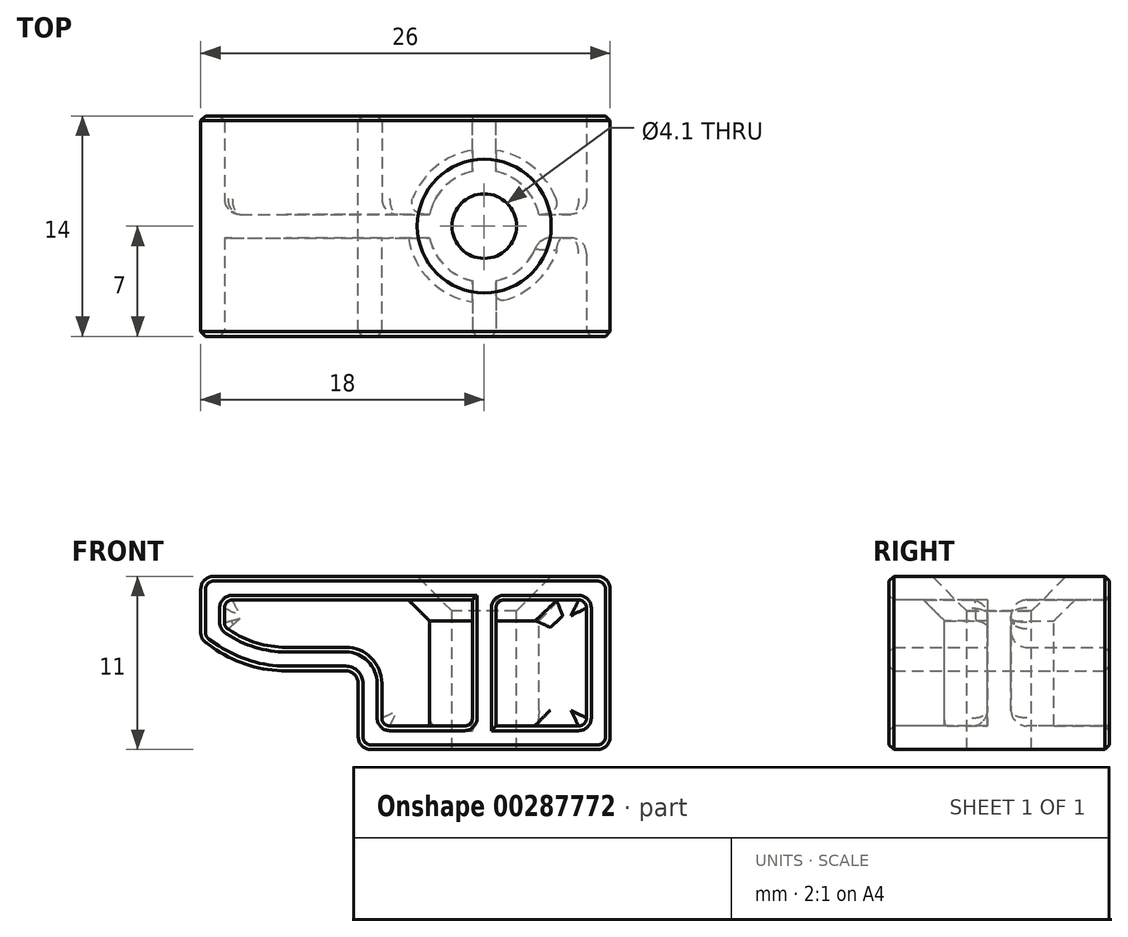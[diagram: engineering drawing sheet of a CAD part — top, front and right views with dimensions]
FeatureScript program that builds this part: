
annotation { "Feature Type Name" : "Feature", "Feature Type Description" : "" }
export const myFeature = defineFeature(function(context is Context, id is Id, definition is map)
    precondition{}
    {
        {
            var Q0;
            Q0=qCreatedBy(makeId("Front.planeOp"),FACE);
            var sketch = newSketch(context, id + "F0", { "sketchPlane" : qUnion([Q0])});
            skLineSegment(sketch, "E0", {"start": v(0, 0) * mm, "end": v(0, 5) * mm});
            skLineSegment(sketch, "E1", {"start": v(0, 5) * mm, "end": v(-7, 5) * mm});
            skLineSegment(sketch, "E2", {"start": v(-7, 5) * mm, "end": v(-10, 7) * mm});
            skLineSegment(sketch, "E3", {"start": v(-10, 7) * mm, "end": v(-10, 11) * mm});
            skLineSegment(sketch, "E4", {"start": v(-10, 11) * mm, "end": v(16, 11) * mm});
            skLineSegment(sketch, "E5", {"start": v(16, 11) * mm, "end": v(16, 0) * mm});
            skLineSegment(sketch, "E6", {"start": v(16, 0) * mm, "end": v(0, 0) * mm});
            skSolve(sketch);
        }
        {
            var Q0;
            Q0=makeQuery(id+"F0.imprint","IMPRINT",FACE,{"disambiguationData":[TD([[makeQuery(id+"F0.imprint","IMPRINT",EDGE,{"derivedFrom":sQuery(id+"F0.wireOp",EDGE,"E0")}),-1.0]])]});
            extrude(context, id + "F1", {"entities" : qUnion([Q0]), "endBound" : BoundingType.SYMMETRIC, "depth" : 14 * mm});
        }
        {
            var Q0;
            Q0=makeQuery(id+"F1.opExtrude","SWEPT_FACE",FACE,{"disambiguationData":[OSD([sQuery(id+"F0.wireOp",EDGE,"E4")])]});
            var sketch = newSketch(context, id + "F2", { "sketchPlane" : qUnion([Q0])});
            skLineSegment(sketch, "E7", {"start": v(0, 0) * mm, "end": v(16, 0) * mm, "construction": true});
            skLineSegment(sketch, "E8", {"start": v(8, 0) * mm, "end": v(8, 7) * mm, "construction": true});
            skSolve(sketch);
        }
        {
            var Q0;
            Q0=sQuery(id+"F2.wireOp",VERTEX,"E8.start");
            var Q1;
            Q1=makeQuery(id+"F1.opExtrude","SWEPT_BODY",BODY,{"disambiguationData":[OSD([sQuery(id+"F0.wireOp",EDGE,"E0"),sQuery(id+"F0.wireOp",EDGE,"E1"),sQuery(id+"F0.wireOp",EDGE,"E2"),sQuery(id+"F0.wireOp",EDGE,"E3"),sQuery(id+"F0.wireOp",EDGE,"E4"),sQuery(id+"F0.wireOp",EDGE,"E5"),sQuery(id+"F0.wireOp",EDGE,"E6")])]});
            hole(context, id + "F3", {"style" : HoleStyle.C_SINK, "endStyle" : HoleEndStyle.THROUGH, "holeDiameter" : 4.1 * mm, "cSinkDiameter" : 8.5 * mm, "cSinkAngle" : 90 * degree, "tappedDepth" : 12 * mm, "tapClearance" : 3, "locations" : qUnion([Q0]), "scope" : qUnion([Q1])});
        }
        {
            var Q0;
            Q0=makeQuery(id+"F1.opExtrude","SWEPT_EDGE",EDGE,{"disambiguationData":[OSD([sQuery(id+"F0.wireOp",EDGE,"E1"),sQuery(id+"F0.wireOp",EDGE,"E2")])]});
            fillet(context, id + "F4", {"entities" : qUnion([Q0]), "radius" : 8 * mm, "tangentPropagation" : true, "allowEdgeOverflow" : false});
        }
        {
            var Q0;
            Q0=makeQuery(id+"F1.opExtrude","SWEPT_EDGE",EDGE,{"disambiguationData":[OSD([sQuery(id+"F0.wireOp",EDGE,"E2"),sQuery(id+"F0.wireOp",EDGE,"E3")])]});
            var Q1;
            Q1=makeQuery(id+"F1.opExtrude","SWEPT_EDGE",EDGE,{"disambiguationData":[OSD([sQuery(id+"F0.wireOp",EDGE,"E3"),sQuery(id+"F0.wireOp",EDGE,"E4")])]});
            var Q2;
            Q2=makeQuery(id+"F1.opExtrude","SWEPT_EDGE",EDGE,{"disambiguationData":[OSD([sQuery(id+"F0.wireOp",EDGE,"E0"),sQuery(id+"F0.wireOp",EDGE,"E6")])]});
            var Q3;
            Q3=makeQuery(id+"F1.opExtrude","SWEPT_EDGE",EDGE,{"disambiguationData":[OSD([sQuery(id+"F0.wireOp",EDGE,"E0"),sQuery(id+"F0.wireOp",EDGE,"E1")])]});
            var Q4;
            Q4=makeQuery(id+"F1.opExtrude","SWEPT_EDGE",EDGE,{"disambiguationData":[OSD([sQuery(id+"F0.wireOp",EDGE,"E5"),sQuery(id+"F0.wireOp",EDGE,"E6")])]});
            var Q5;
            Q5=makeQuery(id+"F1.opExtrude","SWEPT_EDGE",EDGE,{"disambiguationData":[OSD([sQuery(id+"F0.wireOp",EDGE,"E4"),sQuery(id+"F0.wireOp",EDGE,"E5")])]});
            fillet(context, id + "F5", {"entities" : qUnion([Q0, Q1, Q2, Q3, Q4, Q5]), "radius" : 0.8 * mm, "tangentPropagation" : true, "allowEdgeOverflow" : false});
        }
        {
            var Q0;
            Q0=makeQuery(id+"F1.opExtrude","CAP_FACE",FACE,{"disambiguationData":[OSD([sQuery(id+"F0.wireOp",EDGE,"E0"),sQuery(id+"F0.wireOp",EDGE,"E1"),sQuery(id+"F0.wireOp",EDGE,"E2"),sQuery(id+"F0.wireOp",EDGE,"E3"),sQuery(id+"F0.wireOp",EDGE,"E4"),sQuery(id+"F0.wireOp",EDGE,"E5"),sQuery(id+"F0.wireOp",EDGE,"E6")])],"isStart":true});
            shell(context, id + "F6", {"entities" : qUnion([Q0]), "thickness" : 1.5 * mm});
        }
        {
            var Q0;
            Q0=makeQuery(id+"F6.opShell","OFFSET_FACE",FACE,{"disambiguationData":[OSD([sQuery(id+"F0.wireOp",EDGE,"E0"),sQuery(id+"F0.wireOp",EDGE,"E1"),sQuery(id+"F0.wireOp",EDGE,"E2"),sQuery(id+"F0.wireOp",EDGE,"E3"),sQuery(id+"F0.wireOp",EDGE,"E4"),sQuery(id+"F0.wireOp",EDGE,"E5"),sQuery(id+"F0.wireOp",EDGE,"E6")])]});
            var Q1;
            Q1=makeQuery(id+"F1.opExtrude","CAP_FACE",FACE,{"disambiguationData":[OSD([sQuery(id+"F0.wireOp",EDGE,"E0"),sQuery(id+"F0.wireOp",EDGE,"E1"),sQuery(id+"F0.wireOp",EDGE,"E2"),sQuery(id+"F0.wireOp",EDGE,"E3"),sQuery(id+"F0.wireOp",EDGE,"E4"),sQuery(id+"F0.wireOp",EDGE,"E5"),sQuery(id+"F0.wireOp",EDGE,"E6")])],"isStart":false});
            extrude(context, id + "F7", {"entities" : qUnion([Q0, Q1]), "operationType" : NewBodyOperationType.REMOVE, "oppositeDirection" : true, "depth" : 25 * mm});
        }
        {
            var Q0;
            Q0=makeQuery(id+"F1.opExtrude","CAP_FACE",FACE,{"disambiguationData":[OSD([sQuery(id+"F0.wireOp",EDGE,"E0"),sQuery(id+"F0.wireOp",EDGE,"E1"),sQuery(id+"F0.wireOp",EDGE,"E2"),sQuery(id+"F0.wireOp",EDGE,"E3"),sQuery(id+"F0.wireOp",EDGE,"E4"),sQuery(id+"F0.wireOp",EDGE,"E5"),sQuery(id+"F0.wireOp",EDGE,"E6")])],"isStart":true});
            var sketch = newSketch(context, id + "F8", { "sketchPlane" : qUnion([Q0])});
            skLineSegment(sketch, "E9.bottom", {"start": v(-8.75, 11) * mm, "end": v(-7.25, 11) * mm});
            skLineSegment(sketch, "E9.top", {"start": v(-8.75, 0) * mm, "end": v(-7.25, 0) * mm});
            skLineSegment(sketch, "E9.left", {"start": v(-8.75, 11) * mm, "end": v(-8.75, 0) * mm});
            skLineSegment(sketch, "E9.right", {"start": v(-7.25, 11) * mm, "end": v(-7.25, 0) * mm});
            skLineSegment(sketch, "E10", {"start": v(-8, 1.5) * mm, "end": v(-8, 9.5) * mm, "construction": true});
            skSolve(sketch);
        }
        {
            var Q0;
            {var subQ0=sQuery(id+"F8.wireOp",EDGE,"E9.left");var subQ1=sQuery(id+"F0.wireOp",EDGE,"E4");var subQ2=makeQuery(id+"F6.opShell","OFFSET_EDGE",EDGE,{"disambiguationData":[OSD([subQ1]),TDD([makeQuery(id+"F1.opExtrude","CAP_EDGE",EDGE,{"disambiguationData":[OSD([subQ1])],"isStart":true})])]});var subQ3=makeQuery(id+"F8.imprint","INTERSECT",VERTEX,{"derivedFrom":[subQ2,subQ0]});Q0=makeQuery(id+"F8.imprint","IMPRINT",FACE,{"disambiguationData":[TD([[makeQuery(id+"F8.imprint","IMPRINT",EDGE,{"disambiguationData":[TD([[subQ3,-1.0]])],"derivedFrom":subQ0}),1.0]])]});}
            var Q1;
            Q1=makeQuery(id+"F1.opExtrude","SWEPT_BODY",BODY,{"disambiguationData":[OSD([sQuery(id+"F0.wireOp",EDGE,"E0"),sQuery(id+"F0.wireOp",EDGE,"E1"),sQuery(id+"F0.wireOp",EDGE,"E2"),sQuery(id+"F0.wireOp",EDGE,"E3"),sQuery(id+"F0.wireOp",EDGE,"E4"),sQuery(id+"F0.wireOp",EDGE,"E5"),sQuery(id+"F0.wireOp",EDGE,"E6")])]});
            extrude(context, id + "F9", {"entities" : qUnion([Q0]), "operationType" : NewBodyOperationType.ADD, "endBound" : BoundingType.UP_TO_BODY, "oppositeDirection" : true, "endBoundEntityBody" : qUnion([Q1]), "depth" : 25 * mm});
        }
        {
            var Q0;
            Q0=makeQuery(id+"F1.opExtrude","CAP_FACE",FACE,{"disambiguationData":[OSD([sQuery(id+"F0.wireOp",EDGE,"E0"),sQuery(id+"F0.wireOp",EDGE,"E1"),sQuery(id+"F0.wireOp",EDGE,"E2"),sQuery(id+"F0.wireOp",EDGE,"E3"),sQuery(id+"F0.wireOp",EDGE,"E4"),sQuery(id+"F0.wireOp",EDGE,"E5"),sQuery(id+"F0.wireOp",EDGE,"E6")])],"isStart":false});
            var sketch = newSketch(context, id + "F10", { "sketchPlane" : qUnion([Q0])});
            skLineSegment(sketch, "E11", {"start": v(8, 1.5) * mm, "end": v(8, 9.5) * mm, "construction": true});
            skLineSegment(sketch, "E12.bottom", {"start": v(7.25, 11) * mm, "end": v(8.75, 11) * mm});
            skLineSegment(sketch, "E12.top", {"start": v(7.25, 0) * mm, "end": v(8.75, 0) * mm});
            skLineSegment(sketch, "E12.left", {"start": v(7.25, 11) * mm, "end": v(7.25, 0) * mm});
            skLineSegment(sketch, "E12.right", {"start": v(8.75, 11) * mm, "end": v(8.75, 0) * mm});
            skSolve(sketch);
        }
        {
            var Q0;
            {var subQ0=sQuery(id+"F10.wireOp",EDGE,"E12.left");var subQ1=sQuery(id+"F0.wireOp",EDGE,"E4");var subQ2=sQuery(id+"F0.wireOp",EDGE,"E6");var subQ3=sQuery(id+"F0.wireOp",EDGE,"E5");var subQ4=sQuery(id+"F0.wireOp",EDGE,"E3");var subQ5=sQuery(id+"F0.wireOp",EDGE,"E2");var subQ6=sQuery(id+"F0.wireOp",EDGE,"E1");var subQ7=sQuery(id+"F0.wireOp",EDGE,"E0");var subQ8=makeQuery(id+"F1.opExtrude","CAP_FACE",FACE,{"disambiguationData":[OSD([subQ7,subQ6,subQ5,subQ4,subQ1,subQ3,subQ2])],"isStart":false});var subQ9=makeQuery(id+"F7.opExtrude","CAP_FACE",FACE,{"disambiguationData":[OSD([subQ7,subQ6,subQ5,subQ4,subQ1,subQ3,subQ2]),TDD([subQ8])],"isStart":true});var subQ10=makeQuery(id+"F7.boolean.opBoolean","INTERSECT",EDGE,{"derivedFrom":[subQ8,subQ9,makeQuery(id+"F7.opExtrude","SWEPT_FACE",FACE,{"disambiguationData":[OSD([subQ1]),TDD([makeQuery(id+"F6.opShell","OFFSET_EDGE",EDGE,{"disambiguationData":[OSD([subQ1]),TDD([makeQuery(id+"F1.opExtrude","CAP_EDGE",EDGE,{"disambiguationData":[OSD([subQ1])],"isStart":false})])]})])]})]});var subQ11=makeQuery(id+"F10.imprint","INTERSECT",VERTEX,{"derivedFrom":[subQ10,subQ0]});Q0=makeQuery(id+"F10.imprint","IMPRINT",FACE,{"disambiguationData":[TD([[makeQuery(id+"F10.imprint","IMPRINT",EDGE,{"disambiguationData":[TD([[subQ11,-1.0]])],"derivedFrom":subQ0}),1.0]])]});}
            var Q1;
            Q1=makeQuery(id+"F1.opExtrude","SWEPT_BODY",BODY,{"disambiguationData":[OSD([sQuery(id+"F0.wireOp",EDGE,"E0"),sQuery(id+"F0.wireOp",EDGE,"E1"),sQuery(id+"F0.wireOp",EDGE,"E2"),sQuery(id+"F0.wireOp",EDGE,"E3"),sQuery(id+"F0.wireOp",EDGE,"E4"),sQuery(id+"F0.wireOp",EDGE,"E5"),sQuery(id+"F0.wireOp",EDGE,"E6")])]});
            extrude(context, id + "F11", {"entities" : qUnion([Q0]), "operationType" : NewBodyOperationType.ADD, "endBound" : BoundingType.UP_TO_BODY, "oppositeDirection" : true, "endBoundEntityBody" : qUnion([Q1]), "depth" : 25 * mm});
        }
        {
            var Q0;
            Q0=makeQuery(id+"F1.opExtrude","SWEPT_FACE",FACE,{"disambiguationData":[OSD([sQuery(id+"F0.wireOp",EDGE,"E3")])]});
            var sketch = newSketch(context, id + "F12", { "sketchPlane" : qUnion([Q0])});
            skLineSegment(sketch, "E13.bottom", {"start": v(-0.75, 0) * mm, "end": v(0.75, 0) * mm});
            skLineSegment(sketch, "E13.top", {"start": v(-0.75, 11) * mm, "end": v(0.75, 11) * mm});
            skLineSegment(sketch, "E13.left", {"start": v(-0.75, 0) * mm, "end": v(-0.75, 11) * mm});
            skLineSegment(sketch, "E13.right", {"start": v(0.75, 0) * mm, "end": v(0.75, 11) * mm});
            skPoint(sketch, "E13.middle", {"position": v(0, 5.5) * mm});
            skPoint(sketch, "E13.middle.positionSnap0", {"position": v(0, 10.2) * mm});
            skPoint(sketch, "E13.centerSnap0", {"position": v(0, 10.2) * mm});
            skSolve(sketch);
        }
        {
            var Q0;
            {var subQ0=sQuery(id+"F12.wireOp",EDGE,"E13.left");var subQ1=sQuery(id+"F0.wireOp",EDGE,"E3");var subQ2=makeQuery(id+"F1.opExtrude","SWEPT_FACE",FACE,{"disambiguationData":[OSD([subQ1])]});var subQ3=makeQuery(id+"F5.opFillet","BLEND_EDGE",EDGE,{"blendedFrom":[makeQuery(id+"F1.opExtrude","SWEPT_EDGE",EDGE,{"disambiguationData":[OSD([sQuery(id+"F0.wireOp",EDGE,"E2"),subQ1])]}),subQ2],"blendedInto":[subQ2]});var subQ4=makeQuery(id+"F12.imprint","INTERSECT",VERTEX,{"derivedFrom":[subQ3,subQ0]});Q0=makeQuery(id+"F12.imprint","IMPRINT",FACE,{"disambiguationData":[TD([[makeQuery(id+"F12.imprint","IMPRINT",EDGE,{"disambiguationData":[TD([[subQ4,-1.0]])],"derivedFrom":subQ0}),-1.0]])]});}
            var Q1;
            {var subQ0=sQuery(id+"F12.wireOp",EDGE,"E13.bottom");Q1=makeQuery(id+"F12.imprint","IMPRINT",FACE,{"disambiguationData":[TD([[makeQuery(id+"F12.imprint","IMPRINT",EDGE,{"derivedFrom":subQ0}),1.0]])]});}
            var Q2;
            Q2=makeQuery(id+"F1.opExtrude","SWEPT_BODY",BODY,{"disambiguationData":[OSD([sQuery(id+"F0.wireOp",EDGE,"E0"),sQuery(id+"F0.wireOp",EDGE,"E1"),sQuery(id+"F0.wireOp",EDGE,"E2"),sQuery(id+"F0.wireOp",EDGE,"E3"),sQuery(id+"F0.wireOp",EDGE,"E4"),sQuery(id+"F0.wireOp",EDGE,"E5"),sQuery(id+"F0.wireOp",EDGE,"E6")])]});
            extrude(context, id + "F13", {"entities" : qUnion([Q0, Q1]), "operationType" : NewBodyOperationType.ADD, "endBound" : BoundingType.UP_TO_BODY, "oppositeDirection" : true, "endBoundEntityBody" : qUnion([Q2]), "depth" : 25 * mm});
        }
        {
            var Q0;
            {var subQ3=sQuery(id+"F0.wireOp",EDGE,"E0");var subQ6=sQuery(id+"F12.wireOp",EDGE,"E13.right");Q0=makeQuery(id+"F13.boolean.opBoolean","SPLIT",FACE,{"disambiguationData":[TD([makeQuery(id+"F1.opExtrude","SWEPT_FACE",FACE,{"disambiguationData":[OSD([subQ3])]})])],"derivedFrom":makeQuery(id+"F13.opExtrude","SWEPT_FACE",FACE,{"disambiguationData":[OSD([subQ6])]})});}
            var Q1;
            {var subQ3=sQuery(id+"F0.wireOp",EDGE,"E0");var subQ6=sQuery(id+"F12.wireOp",EDGE,"E13.left");Q1=makeQuery(id+"F13.boolean.opBoolean","SPLIT",FACE,{"disambiguationData":[TD([makeQuery(id+"F1.opExtrude","SWEPT_FACE",FACE,{"disambiguationData":[OSD([subQ3])]})])],"derivedFrom":makeQuery(id+"F13.opExtrude","SWEPT_FACE",FACE,{"disambiguationData":[OSD([subQ6])]})});}
            extrude(context, id + "F14", {"entities" : qUnion([Q0]), "operationType" : NewBodyOperationType.REMOVE, "endBound" : BoundingType.UP_TO_SURFACE, "oppositeDirection" : true, "endBoundEntityFace" : qUnion([Q1]), "depth" : 25 * mm});
        }
        {
            var Q0;
            Q0=makeQuery(id+"F1.opExtrude","SWEPT_FACE",FACE,{"disambiguationData":[OSD([sQuery(id+"F0.wireOp",EDGE,"E5")])]});
            var sketch = newSketch(context, id + "F15", { "sketchPlane" : qUnion([Q0])});
            skLineSegment(sketch, "E14.bottom", {"start": v(-0.75, 11) * mm, "end": v(0.75, 11) * mm});
            skLineSegment(sketch, "E14.top", {"start": v(-0.75, 0) * mm, "end": v(0.75, 0) * mm});
            skLineSegment(sketch, "E14.left", {"start": v(-0.75, 11) * mm, "end": v(-0.75, 0) * mm});
            skLineSegment(sketch, "E14.right", {"start": v(0.75, 11) * mm, "end": v(0.75, 0) * mm});
            skPoint(sketch, "E14.middle", {"position": v(0, 5.5) * mm});
            skSolve(sketch);
        }
        {
            var Q0;
            {var subQ0=sQuery(id+"F15.wireOp",EDGE,"E14.left");var subQ1=sQuery(id+"F0.wireOp",EDGE,"E5");var subQ2=makeQuery(id+"F1.opExtrude","SWEPT_FACE",FACE,{"disambiguationData":[OSD([subQ1])]});var subQ3=makeQuery(id+"F5.opFillet","BLEND_EDGE",EDGE,{"blendedFrom":[makeQuery(id+"F1.opExtrude","SWEPT_EDGE",EDGE,{"disambiguationData":[OSD([sQuery(id+"F0.wireOp",EDGE,"E4"),subQ1])]}),subQ2],"blendedInto":[subQ2]});var subQ4=makeQuery(id+"F15.imprint","INTERSECT",VERTEX,{"derivedFrom":[subQ3,subQ0]});Q0=makeQuery(id+"F15.imprint","IMPRINT",FACE,{"disambiguationData":[TD([[makeQuery(id+"F15.imprint","IMPRINT",EDGE,{"disambiguationData":[TD([[subQ4,-1.0]])],"derivedFrom":subQ0}),1.0]])]});}
            var Q1;
            Q1=makeQuery(id+"F1.opExtrude","SWEPT_BODY",BODY,{"disambiguationData":[OSD([sQuery(id+"F0.wireOp",EDGE,"E0"),sQuery(id+"F0.wireOp",EDGE,"E1"),sQuery(id+"F0.wireOp",EDGE,"E2"),sQuery(id+"F0.wireOp",EDGE,"E3"),sQuery(id+"F0.wireOp",EDGE,"E4"),sQuery(id+"F0.wireOp",EDGE,"E5"),sQuery(id+"F0.wireOp",EDGE,"E6")])]});
            extrude(context, id + "F16", {"entities" : qUnion([Q0]), "operationType" : NewBodyOperationType.ADD, "endBound" : BoundingType.UP_TO_BODY, "oppositeDirection" : true, "endBoundEntityBody" : qUnion([Q1]), "depth" : 25 * mm});
        }
        {
            var Q0;
            {var subQ0=sQuery(id+"F0.wireOp",EDGE,"E6");var subQ1=sQuery(id+"F0.wireOp",EDGE,"E5");var subQ2=sQuery(id+"F0.wireOp",EDGE,"E4");var subQ3=sQuery(id+"F0.wireOp",EDGE,"E3");var subQ4=sQuery(id+"F0.wireOp",EDGE,"E2");var subQ5=sQuery(id+"F0.wireOp",EDGE,"E1");var subQ6=sQuery(id+"F0.wireOp",EDGE,"E0");var subQ7=makeQuery(id+"F1.opExtrude","CAP_FACE",FACE,{"disambiguationData":[OSD([subQ6,subQ5,subQ4,subQ3,subQ2,subQ1,subQ0])],"isStart":false});var subQ8=subQ7;var subQ9=makeQuery(id+"F1.opExtrude","SWEPT_EDGE",EDGE,{"disambiguationData":[OSD([subQ3,subQ2])]});Q0=makeQuery(id+"F13.boolean.opBoolean","SPLIT",EDGE,{"disambiguationData":[TD([makeQuery(id+"F13.opExtrude","SWEPT_FACE",FACE,{"disambiguationData":[OSD([sQuery(id+"F12.wireOp",EDGE,"E13.right")])]})])],"derivedFrom":makeQuery(id+"F7.boolean.opBoolean","MERGE",EDGE,{"derivedFrom":[makeQuery(id+"F6.opShell","OFFSET_EDGE",EDGE,{"disambiguationData":[OSD([subQ3,subQ2])]})],"fromTools":[makeQuery(id+"F7.opExtrude","SWEPT_EDGE",EDGE,{"disambiguationData":[OSD([subQ6,subQ5,subQ4,subQ3,subQ2,subQ1,subQ0]),TDD([makeQuery(id+"F6.opShell","OFFSET_VERTEX",VERTEX,{"disambiguationData":[OSD([subQ6,subQ5,subQ4,subQ3,subQ2,subQ1,subQ0]),TDD([makeQuery(id+"F5.opFillet","BLEND_VERTEX",VERTEX,{"blendedFrom":[subQ9,makeQuery(id+"F1.opExtrude","SWEPT_FACE",FACE,{"disambiguationData":[OSD([subQ3])]}),subQ8],"blendedInto":[makeQuery(id+"F1.opExtrude","SWEPT_FACE",FACE,{"disambiguationData":[OSD([subQ3])]}),subQ8]}),makeQuery(id+"F5.opFillet","BLEND_VERTEX",VERTEX,{"blendedFrom":[subQ9,makeQuery(id+"F1.opExtrude","SWEPT_FACE",FACE,{"disambiguationData":[OSD([subQ2])]}),subQ8],"blendedInto":[makeQuery(id+"F1.opExtrude","SWEPT_FACE",FACE,{"disambiguationData":[OSD([subQ2])]}),subQ8]})])]})])]})]})});}
            var Q1;
            {var subQ0=sQuery(id+"F0.wireOp",EDGE,"E2");var subQ1=sQuery(id+"F0.wireOp",EDGE,"E6");var subQ2=sQuery(id+"F0.wireOp",EDGE,"E5");var subQ3=sQuery(id+"F0.wireOp",EDGE,"E4");var subQ4=sQuery(id+"F0.wireOp",EDGE,"E3");var subQ5=sQuery(id+"F0.wireOp",EDGE,"E1");var subQ6=sQuery(id+"F0.wireOp",EDGE,"E0");var subQ7=makeQuery(id+"F1.opExtrude","CAP_FACE",FACE,{"disambiguationData":[OSD([subQ6,subQ5,subQ0,subQ4,subQ3,subQ2,subQ1])],"isStart":false});var subQ8=subQ7;var subQ9=makeQuery(id+"F1.opExtrude","SWEPT_EDGE",EDGE,{"disambiguationData":[OSD([subQ0,subQ4])]});Q1=makeQuery(id+"F13.boolean.opBoolean","SPLIT",EDGE,{"disambiguationData":[TD([makeQuery(id+"F13.opExtrude","SWEPT_FACE",FACE,{"disambiguationData":[OSD([sQuery(id+"F12.wireOp",EDGE,"E13.right")])]})])],"derivedFrom":makeQuery(id+"F7.boolean.opBoolean","MERGE",EDGE,{"derivedFrom":[makeQuery(id+"F6.opShell","OFFSET_EDGE",EDGE,{"disambiguationData":[OSD([subQ0,subQ4])]})],"fromTools":[makeQuery(id+"F7.opExtrude","SWEPT_EDGE",EDGE,{"disambiguationData":[OSD([subQ6,subQ5,subQ0,subQ4,subQ3,subQ2,subQ1]),TDD([makeQuery(id+"F6.opShell","OFFSET_VERTEX",VERTEX,{"disambiguationData":[OSD([subQ6,subQ5,subQ0,subQ4,subQ3,subQ2,subQ1]),TDD([makeQuery(id+"F5.opFillet","BLEND_VERTEX",VERTEX,{"blendedFrom":[subQ9,makeQuery(id+"F1.opExtrude","SWEPT_FACE",FACE,{"disambiguationData":[OSD([subQ4])]}),subQ8],"blendedInto":[makeQuery(id+"F1.opExtrude","SWEPT_FACE",FACE,{"disambiguationData":[OSD([subQ4])]}),subQ8]}),makeQuery(id+"F5.opFillet","BLEND_VERTEX",VERTEX,{"blendedFrom":[subQ9,subQ8,makeQuery(id+"F1.opExtrude","SWEPT_FACE",FACE,{"disambiguationData":[OSD([subQ0])]})],"blendedInto":[subQ8,makeQuery(id+"F1.opExtrude","SWEPT_FACE",FACE,{"disambiguationData":[OSD([subQ0])]})]})])]})])]})]})});}
            var Q2;
            {var subQ0=sQuery(id+"F10.wireOp",EDGE,"E12.left");var subQ1=sQuery(id+"F0.wireOp",EDGE,"E4");var subQ2=sQuery(id+"F0.wireOp",EDGE,"E6");var subQ3=sQuery(id+"F0.wireOp",EDGE,"E5");var subQ4=sQuery(id+"F0.wireOp",EDGE,"E3");var subQ5=sQuery(id+"F0.wireOp",EDGE,"E2");var subQ6=sQuery(id+"F0.wireOp",EDGE,"E1");var subQ7=sQuery(id+"F0.wireOp",EDGE,"E0");var subQ8=makeQuery(id+"F1.opExtrude","CAP_FACE",FACE,{"disambiguationData":[OSD([subQ7,subQ6,subQ5,subQ4,subQ1,subQ3,subQ2])],"isStart":false});Q2=makeQuery(id+"F11.opExtrude","SWEPT_EDGE",EDGE,{"disambiguationData":[OSD([subQ7,subQ6,subQ5,subQ4,subQ1,subQ3,subQ2,subQ0]),TDD([makeQuery(id+"F10.imprint","INTERSECT",VERTEX,{"derivedFrom":[makeQuery(id+"F7.boolean.opBoolean","INTERSECT",EDGE,{"derivedFrom":[subQ8,makeQuery(id+"F7.opExtrude","CAP_FACE",FACE,{"disambiguationData":[OSD([subQ7,subQ6,subQ5,subQ4,subQ1,subQ3,subQ2]),TDD([subQ8])],"isStart":true}),makeQuery(id+"F7.opExtrude","SWEPT_FACE",FACE,{"disambiguationData":[OSD([subQ1]),TDD([makeQuery(id+"F6.opShell","OFFSET_EDGE",EDGE,{"disambiguationData":[OSD([subQ1]),TDD([makeQuery(id+"F1.opExtrude","CAP_EDGE",EDGE,{"disambiguationData":[OSD([subQ1])],"isStart":false})])]})])]})]}),subQ0]})])]});}
            var Q3;
            {var subQ0=sQuery(id+"F10.wireOp",EDGE,"E12.right");var subQ1=sQuery(id+"F0.wireOp",EDGE,"E4");var subQ2=sQuery(id+"F0.wireOp",EDGE,"E6");var subQ3=sQuery(id+"F0.wireOp",EDGE,"E5");var subQ4=sQuery(id+"F0.wireOp",EDGE,"E3");var subQ5=sQuery(id+"F0.wireOp",EDGE,"E2");var subQ6=sQuery(id+"F0.wireOp",EDGE,"E1");var subQ7=sQuery(id+"F0.wireOp",EDGE,"E0");var subQ8=makeQuery(id+"F1.opExtrude","CAP_FACE",FACE,{"disambiguationData":[OSD([subQ7,subQ6,subQ5,subQ4,subQ1,subQ3,subQ2])],"isStart":false});Q3=makeQuery(id+"F11.opExtrude","SWEPT_EDGE",EDGE,{"disambiguationData":[OSD([subQ7,subQ6,subQ5,subQ4,subQ1,subQ3,subQ2,subQ0]),TDD([makeQuery(id+"F10.imprint","INTERSECT",VERTEX,{"derivedFrom":[makeQuery(id+"F7.boolean.opBoolean","INTERSECT",EDGE,{"derivedFrom":[subQ8,makeQuery(id+"F7.opExtrude","CAP_FACE",FACE,{"disambiguationData":[OSD([subQ7,subQ6,subQ5,subQ4,subQ1,subQ3,subQ2]),TDD([subQ8])],"isStart":true}),makeQuery(id+"F7.opExtrude","SWEPT_FACE",FACE,{"disambiguationData":[OSD([subQ1]),TDD([makeQuery(id+"F6.opShell","OFFSET_EDGE",EDGE,{"disambiguationData":[OSD([subQ1]),TDD([makeQuery(id+"F1.opExtrude","CAP_EDGE",EDGE,{"disambiguationData":[OSD([subQ1])],"isStart":false})])]})])]})]}),subQ0]})])]});}
            var Q4;
            {var subQ0=sQuery(id+"F0.wireOp",EDGE,"E6");var subQ1=sQuery(id+"F0.wireOp",EDGE,"E5");var subQ2=sQuery(id+"F0.wireOp",EDGE,"E4");var subQ3=sQuery(id+"F0.wireOp",EDGE,"E3");var subQ4=sQuery(id+"F0.wireOp",EDGE,"E2");var subQ5=sQuery(id+"F0.wireOp",EDGE,"E1");var subQ6=sQuery(id+"F0.wireOp",EDGE,"E0");var subQ7=makeQuery(id+"F1.opExtrude","CAP_FACE",FACE,{"disambiguationData":[OSD([subQ6,subQ5,subQ4,subQ3,subQ2,subQ1,subQ0])],"isStart":false});var subQ8=subQ7;var subQ9=makeQuery(id+"F1.opExtrude","SWEPT_EDGE",EDGE,{"disambiguationData":[OSD([subQ6,subQ0])]});Q4=makeQuery(id+"F13.boolean.opBoolean","SPLIT",EDGE,{"disambiguationData":[TD([makeQuery(id+"F13.opExtrude","SWEPT_FACE",FACE,{"disambiguationData":[OSD([sQuery(id+"F12.wireOp",EDGE,"E13.right")])]})])],"derivedFrom":makeQuery(id+"F7.boolean.opBoolean","MERGE",EDGE,{"derivedFrom":[makeQuery(id+"F6.opShell","OFFSET_EDGE",EDGE,{"disambiguationData":[OSD([subQ6,subQ0])]})],"fromTools":[makeQuery(id+"F7.opExtrude","SWEPT_EDGE",EDGE,{"disambiguationData":[OSD([subQ6,subQ5,subQ4,subQ3,subQ2,subQ1,subQ0]),TDD([makeQuery(id+"F6.opShell","OFFSET_VERTEX",VERTEX,{"disambiguationData":[OSD([subQ6,subQ5,subQ4,subQ3,subQ2,subQ1,subQ0]),TDD([makeQuery(id+"F5.opFillet","BLEND_VERTEX",VERTEX,{"blendedFrom":[subQ9,makeQuery(id+"F1.opExtrude","SWEPT_FACE",FACE,{"disambiguationData":[OSD([subQ6])]}),subQ8],"blendedInto":[makeQuery(id+"F1.opExtrude","SWEPT_FACE",FACE,{"disambiguationData":[OSD([subQ6])]}),subQ8]}),makeQuery(id+"F5.opFillet","BLEND_VERTEX",VERTEX,{"blendedFrom":[subQ9,makeQuery(id+"F1.opExtrude","SWEPT_FACE",FACE,{"disambiguationData":[OSD([subQ0])]}),subQ8],"blendedInto":[makeQuery(id+"F1.opExtrude","SWEPT_FACE",FACE,{"disambiguationData":[OSD([subQ0])]}),subQ8]})])]})])]})]})});}
            var Q5;
            {var subQ0=sQuery(id+"F10.wireOp",EDGE,"E12.left");var subQ1=sQuery(id+"F0.wireOp",EDGE,"E6");var subQ2=sQuery(id+"F0.wireOp",EDGE,"E5");var subQ3=sQuery(id+"F0.wireOp",EDGE,"E4");var subQ4=sQuery(id+"F0.wireOp",EDGE,"E3");var subQ5=sQuery(id+"F0.wireOp",EDGE,"E2");var subQ6=sQuery(id+"F0.wireOp",EDGE,"E1");var subQ7=sQuery(id+"F0.wireOp",EDGE,"E0");var subQ8=makeQuery(id+"F1.opExtrude","CAP_FACE",FACE,{"disambiguationData":[OSD([subQ7,subQ6,subQ5,subQ4,subQ3,subQ2,subQ1])],"isStart":false});Q5=makeQuery(id+"F11.opExtrude","SWEPT_EDGE",EDGE,{"disambiguationData":[OSD([subQ7,subQ6,subQ5,subQ4,subQ3,subQ2,subQ1,subQ0]),TDD([makeQuery(id+"F10.imprint","INTERSECT",VERTEX,{"derivedFrom":[makeQuery(id+"F7.boolean.opBoolean","INTERSECT",EDGE,{"derivedFrom":[subQ8,makeQuery(id+"F7.opExtrude","CAP_FACE",FACE,{"disambiguationData":[OSD([subQ7,subQ6,subQ5,subQ4,subQ3,subQ2,subQ1]),TDD([subQ8])],"isStart":true}),makeQuery(id+"F7.opExtrude","SWEPT_FACE",FACE,{"disambiguationData":[OSD([subQ1]),TDD([makeQuery(id+"F6.opShell","OFFSET_EDGE",EDGE,{"disambiguationData":[OSD([subQ1]),TDD([makeQuery(id+"F1.opExtrude","CAP_EDGE",EDGE,{"disambiguationData":[OSD([subQ1])],"isStart":false})])]})])]})]}),subQ0]})])]});}
            var Q6;
            {var subQ0=sQuery(id+"F10.wireOp",EDGE,"E12.right");var subQ1=sQuery(id+"F0.wireOp",EDGE,"E6");var subQ2=sQuery(id+"F0.wireOp",EDGE,"E5");var subQ3=sQuery(id+"F0.wireOp",EDGE,"E4");var subQ4=sQuery(id+"F0.wireOp",EDGE,"E3");var subQ5=sQuery(id+"F0.wireOp",EDGE,"E2");var subQ6=sQuery(id+"F0.wireOp",EDGE,"E1");var subQ7=sQuery(id+"F0.wireOp",EDGE,"E0");var subQ8=makeQuery(id+"F1.opExtrude","CAP_FACE",FACE,{"disambiguationData":[OSD([subQ7,subQ6,subQ5,subQ4,subQ3,subQ2,subQ1])],"isStart":false});Q6=makeQuery(id+"F11.opExtrude","SWEPT_EDGE",EDGE,{"disambiguationData":[OSD([subQ7,subQ6,subQ5,subQ4,subQ3,subQ2,subQ1,subQ0]),TDD([makeQuery(id+"F10.imprint","INTERSECT",VERTEX,{"derivedFrom":[makeQuery(id+"F7.boolean.opBoolean","INTERSECT",EDGE,{"derivedFrom":[subQ8,makeQuery(id+"F7.opExtrude","CAP_FACE",FACE,{"disambiguationData":[OSD([subQ7,subQ6,subQ5,subQ4,subQ3,subQ2,subQ1]),TDD([subQ8])],"isStart":true}),makeQuery(id+"F7.opExtrude","SWEPT_FACE",FACE,{"disambiguationData":[OSD([subQ1]),TDD([makeQuery(id+"F6.opShell","OFFSET_EDGE",EDGE,{"disambiguationData":[OSD([subQ1]),TDD([makeQuery(id+"F1.opExtrude","CAP_EDGE",EDGE,{"disambiguationData":[OSD([subQ1])],"isStart":false})])]})])]})]}),subQ0]})])]});}
            var Q7;
            {var subQ0=sQuery(id+"F0.wireOp",EDGE,"E6");var subQ1=sQuery(id+"F0.wireOp",EDGE,"E5");var subQ2=sQuery(id+"F0.wireOp",EDGE,"E4");var subQ3=sQuery(id+"F0.wireOp",EDGE,"E3");var subQ4=sQuery(id+"F0.wireOp",EDGE,"E2");var subQ5=sQuery(id+"F0.wireOp",EDGE,"E1");var subQ6=sQuery(id+"F0.wireOp",EDGE,"E0");var subQ7=makeQuery(id+"F1.opExtrude","CAP_FACE",FACE,{"disambiguationData":[OSD([subQ6,subQ5,subQ4,subQ3,subQ2,subQ1,subQ0])],"isStart":false});var subQ8=subQ7;var subQ9=makeQuery(id+"F1.opExtrude","SWEPT_EDGE",EDGE,{"disambiguationData":[OSD([subQ1,subQ0])]});Q7=makeQuery(id+"F16.boolean.opBoolean","SPLIT",EDGE,{"disambiguationData":[TD([makeQuery(id+"F16.opExtrude","SWEPT_FACE",FACE,{"disambiguationData":[OSD([sQuery(id+"F15.wireOp",EDGE,"E14.left")])]})])],"derivedFrom":makeQuery(id+"F7.boolean.opBoolean","MERGE",EDGE,{"derivedFrom":[makeQuery(id+"F6.opShell","OFFSET_EDGE",EDGE,{"disambiguationData":[OSD([subQ1,subQ0])]})],"fromTools":[makeQuery(id+"F7.opExtrude","SWEPT_EDGE",EDGE,{"disambiguationData":[OSD([subQ6,subQ5,subQ4,subQ3,subQ2,subQ1,subQ0]),TDD([makeQuery(id+"F6.opShell","OFFSET_VERTEX",VERTEX,{"disambiguationData":[OSD([subQ6,subQ5,subQ4,subQ3,subQ2,subQ1,subQ0]),TDD([makeQuery(id+"F5.opFillet","BLEND_VERTEX",VERTEX,{"blendedFrom":[subQ9,makeQuery(id+"F1.opExtrude","SWEPT_FACE",FACE,{"disambiguationData":[OSD([subQ1])]}),subQ8],"blendedInto":[makeQuery(id+"F1.opExtrude","SWEPT_FACE",FACE,{"disambiguationData":[OSD([subQ1])]}),subQ8]}),makeQuery(id+"F5.opFillet","BLEND_VERTEX",VERTEX,{"blendedFrom":[subQ9,makeQuery(id+"F1.opExtrude","SWEPT_FACE",FACE,{"disambiguationData":[OSD([subQ0])]}),subQ8],"blendedInto":[makeQuery(id+"F1.opExtrude","SWEPT_FACE",FACE,{"disambiguationData":[OSD([subQ0])]}),subQ8]})])]})])]})]})});}
            var Q8;
            {var subQ0=sQuery(id+"F0.wireOp",EDGE,"E6");var subQ1=sQuery(id+"F0.wireOp",EDGE,"E5");var subQ2=sQuery(id+"F0.wireOp",EDGE,"E4");var subQ3=sQuery(id+"F0.wireOp",EDGE,"E3");var subQ4=sQuery(id+"F0.wireOp",EDGE,"E2");var subQ5=sQuery(id+"F0.wireOp",EDGE,"E1");var subQ6=sQuery(id+"F0.wireOp",EDGE,"E0");var subQ7=makeQuery(id+"F1.opExtrude","CAP_FACE",FACE,{"disambiguationData":[OSD([subQ6,subQ5,subQ4,subQ3,subQ2,subQ1,subQ0])],"isStart":false});var subQ8=subQ7;var subQ9=makeQuery(id+"F1.opExtrude","SWEPT_EDGE",EDGE,{"disambiguationData":[OSD([subQ2,subQ1])]});Q8=makeQuery(id+"F16.boolean.opBoolean","SPLIT",EDGE,{"disambiguationData":[TD([makeQuery(id+"F16.opExtrude","SWEPT_FACE",FACE,{"disambiguationData":[OSD([sQuery(id+"F15.wireOp",EDGE,"E14.left")])]})])],"derivedFrom":makeQuery(id+"F7.boolean.opBoolean","MERGE",EDGE,{"derivedFrom":[makeQuery(id+"F6.opShell","OFFSET_EDGE",EDGE,{"disambiguationData":[OSD([subQ2,subQ1])]})],"fromTools":[makeQuery(id+"F7.opExtrude","SWEPT_EDGE",EDGE,{"disambiguationData":[OSD([subQ6,subQ5,subQ4,subQ3,subQ2,subQ1,subQ0]),TDD([makeQuery(id+"F6.opShell","OFFSET_VERTEX",VERTEX,{"disambiguationData":[OSD([subQ6,subQ5,subQ4,subQ3,subQ2,subQ1,subQ0]),TDD([makeQuery(id+"F5.opFillet","BLEND_VERTEX",VERTEX,{"blendedFrom":[subQ9,makeQuery(id+"F1.opExtrude","SWEPT_FACE",FACE,{"disambiguationData":[OSD([subQ1])]}),subQ8],"blendedInto":[makeQuery(id+"F1.opExtrude","SWEPT_FACE",FACE,{"disambiguationData":[OSD([subQ1])]}),subQ8]}),makeQuery(id+"F5.opFillet","BLEND_VERTEX",VERTEX,{"blendedFrom":[subQ9,makeQuery(id+"F1.opExtrude","SWEPT_FACE",FACE,{"disambiguationData":[OSD([subQ2])]}),subQ8],"blendedInto":[makeQuery(id+"F1.opExtrude","SWEPT_FACE",FACE,{"disambiguationData":[OSD([subQ2])]}),subQ8]})])]})])]})]})});}
            var Q9;
            {var subQ0=sQuery(id+"F0.wireOp",EDGE,"E4");var subQ1=sQuery(id+"F0.wireOp",EDGE,"E6");var subQ2=sQuery(id+"F0.wireOp",EDGE,"E5");var subQ3=sQuery(id+"F0.wireOp",EDGE,"E3");var subQ4=sQuery(id+"F0.wireOp",EDGE,"E2");var subQ5=sQuery(id+"F0.wireOp",EDGE,"E1");var subQ6=sQuery(id+"F0.wireOp",EDGE,"E0");var subQ7=makeQuery(id+"F1.opExtrude","CAP_FACE",FACE,{"disambiguationData":[OSD([subQ6,subQ5,subQ4,subQ3,subQ0,subQ2,subQ1])],"isStart":false});var subQ8=makeQuery(id+"F1.opExtrude","SWEPT_EDGE",EDGE,{"disambiguationData":[OSD([subQ0,subQ2])]});Q9=makeQuery(id+"F16.boolean.opBoolean","SPLIT",EDGE,{"disambiguationData":[TD([makeQuery(id+"F16.opExtrude","SWEPT_FACE",FACE,{"disambiguationData":[OSD([sQuery(id+"F15.wireOp",EDGE,"E14.right")])]})])],"derivedFrom":makeQuery(id+"F7.boolean.opBoolean","MERGE",EDGE,{"derivedFrom":[makeQuery(id+"F6.opShell","OFFSET_EDGE",EDGE,{"disambiguationData":[OSD([subQ0,subQ2])]})],"fromTools":[makeQuery(id+"F7.opExtrude","SWEPT_EDGE",EDGE,{"disambiguationData":[OSD([subQ6,subQ5,subQ4,subQ3,subQ0,subQ2,subQ1]),TDD([makeQuery(id+"F6.opShell","OFFSET_VERTEX",VERTEX,{"disambiguationData":[OSD([subQ6,subQ5,subQ4,subQ3,subQ0,subQ2,subQ1]),TDD([makeQuery(id+"F5.opFillet","BLEND_VERTEX",VERTEX,{"blendedFrom":[subQ8,makeQuery(id+"F1.opExtrude","SWEPT_FACE",FACE,{"disambiguationData":[OSD([subQ2])]}),subQ7],"blendedInto":[makeQuery(id+"F1.opExtrude","SWEPT_FACE",FACE,{"disambiguationData":[OSD([subQ2])]}),subQ7]}),makeQuery(id+"F5.opFillet","BLEND_VERTEX",VERTEX,{"blendedFrom":[subQ8,makeQuery(id+"F1.opExtrude","SWEPT_FACE",FACE,{"disambiguationData":[OSD([subQ0])]}),subQ7],"blendedInto":[makeQuery(id+"F1.opExtrude","SWEPT_FACE",FACE,{"disambiguationData":[OSD([subQ0])]}),subQ7]})])]})])]})]})});}
            var Q10;
            Q10=makeQuery(id+"F9.opExtrude","SWEPT_EDGE",EDGE,{"disambiguationData":[OSD([sQuery(id+"F0.wireOp",EDGE,"E4"),sQuery(id+"F8.wireOp",EDGE,"E9.right")])]});
            var Q11;
            {var subQ0=sQuery(id+"F0.wireOp",EDGE,"E4");var subQ1=sQuery(id+"F0.wireOp",EDGE,"E3");var subQ2=sQuery(id+"F0.wireOp",EDGE,"E6");var subQ3=sQuery(id+"F0.wireOp",EDGE,"E5");var subQ4=sQuery(id+"F0.wireOp",EDGE,"E2");var subQ5=sQuery(id+"F0.wireOp",EDGE,"E1");var subQ6=sQuery(id+"F0.wireOp",EDGE,"E0");var subQ7=makeQuery(id+"F1.opExtrude","CAP_FACE",FACE,{"disambiguationData":[OSD([subQ6,subQ5,subQ4,subQ1,subQ0,subQ3,subQ2])],"isStart":false});var subQ8=makeQuery(id+"F1.opExtrude","SWEPT_EDGE",EDGE,{"disambiguationData":[OSD([subQ1,subQ0])]});Q11=makeQuery(id+"F13.boolean.opBoolean","SPLIT",EDGE,{"disambiguationData":[TD([makeQuery(id+"F13.opExtrude","SWEPT_FACE",FACE,{"disambiguationData":[OSD([sQuery(id+"F12.wireOp",EDGE,"E13.left")])]})])],"derivedFrom":makeQuery(id+"F7.boolean.opBoolean","MERGE",EDGE,{"derivedFrom":[makeQuery(id+"F6.opShell","OFFSET_EDGE",EDGE,{"disambiguationData":[OSD([subQ1,subQ0])]})],"fromTools":[makeQuery(id+"F7.opExtrude","SWEPT_EDGE",EDGE,{"disambiguationData":[OSD([subQ6,subQ5,subQ4,subQ1,subQ0,subQ3,subQ2]),TDD([makeQuery(id+"F6.opShell","OFFSET_VERTEX",VERTEX,{"disambiguationData":[OSD([subQ6,subQ5,subQ4,subQ1,subQ0,subQ3,subQ2]),TDD([makeQuery(id+"F5.opFillet","BLEND_VERTEX",VERTEX,{"blendedFrom":[subQ8,makeQuery(id+"F1.opExtrude","SWEPT_FACE",FACE,{"disambiguationData":[OSD([subQ1])]}),subQ7],"blendedInto":[makeQuery(id+"F1.opExtrude","SWEPT_FACE",FACE,{"disambiguationData":[OSD([subQ1])]}),subQ7]}),makeQuery(id+"F5.opFillet","BLEND_VERTEX",VERTEX,{"blendedFrom":[subQ8,makeQuery(id+"F1.opExtrude","SWEPT_FACE",FACE,{"disambiguationData":[OSD([subQ0])]}),subQ7],"blendedInto":[makeQuery(id+"F1.opExtrude","SWEPT_FACE",FACE,{"disambiguationData":[OSD([subQ0])]}),subQ7]})])]})])]})]})});}
            var Q12;
            Q12=makeQuery(id+"F9.opExtrude","SWEPT_EDGE",EDGE,{"disambiguationData":[OSD([sQuery(id+"F0.wireOp",EDGE,"E4"),sQuery(id+"F8.wireOp",EDGE,"E9.left")])]});
            var Q13;
            {var subQ0=sQuery(id+"F0.wireOp",EDGE,"E6");var subQ1=sQuery(id+"F0.wireOp",EDGE,"E4");var subQ2=sQuery(id+"F0.wireOp",EDGE,"E5");var subQ3=sQuery(id+"F0.wireOp",EDGE,"E3");var subQ4=sQuery(id+"F0.wireOp",EDGE,"E2");var subQ5=sQuery(id+"F0.wireOp",EDGE,"E1");var subQ6=sQuery(id+"F0.wireOp",EDGE,"E0");var subQ7=makeQuery(id+"F1.opExtrude","CAP_FACE",FACE,{"disambiguationData":[OSD([subQ6,subQ5,subQ4,subQ3,subQ1,subQ2,subQ0])],"isStart":false});var subQ8=makeQuery(id+"F1.opExtrude","SWEPT_EDGE",EDGE,{"disambiguationData":[OSD([subQ2,subQ0])]});Q13=makeQuery(id+"F16.boolean.opBoolean","SPLIT",EDGE,{"disambiguationData":[TD([makeQuery(id+"F16.opExtrude","SWEPT_FACE",FACE,{"disambiguationData":[OSD([sQuery(id+"F15.wireOp",EDGE,"E14.right")])]})])],"derivedFrom":makeQuery(id+"F7.boolean.opBoolean","MERGE",EDGE,{"derivedFrom":[makeQuery(id+"F6.opShell","OFFSET_EDGE",EDGE,{"disambiguationData":[OSD([subQ2,subQ0])]})],"fromTools":[makeQuery(id+"F7.opExtrude","SWEPT_EDGE",EDGE,{"disambiguationData":[OSD([subQ6,subQ5,subQ4,subQ3,subQ1,subQ2,subQ0]),TDD([makeQuery(id+"F6.opShell","OFFSET_VERTEX",VERTEX,{"disambiguationData":[OSD([subQ6,subQ5,subQ4,subQ3,subQ1,subQ2,subQ0]),TDD([makeQuery(id+"F5.opFillet","BLEND_VERTEX",VERTEX,{"blendedFrom":[subQ8,makeQuery(id+"F1.opExtrude","SWEPT_FACE",FACE,{"disambiguationData":[OSD([subQ2])]}),subQ7],"blendedInto":[makeQuery(id+"F1.opExtrude","SWEPT_FACE",FACE,{"disambiguationData":[OSD([subQ2])]}),subQ7]}),makeQuery(id+"F5.opFillet","BLEND_VERTEX",VERTEX,{"blendedFrom":[subQ8,makeQuery(id+"F1.opExtrude","SWEPT_FACE",FACE,{"disambiguationData":[OSD([subQ0])]}),subQ7],"blendedInto":[makeQuery(id+"F1.opExtrude","SWEPT_FACE",FACE,{"disambiguationData":[OSD([subQ0])]}),subQ7]})])]})])]})]})});}
            var Q14;
            {var subQ0=sQuery(id+"F0.wireOp",EDGE,"E6");var subQ1=sQuery(id+"F0.wireOp",EDGE,"E0");var subQ2=sQuery(id+"F0.wireOp",EDGE,"E4");var subQ3=sQuery(id+"F0.wireOp",EDGE,"E5");var subQ4=sQuery(id+"F0.wireOp",EDGE,"E3");var subQ5=sQuery(id+"F0.wireOp",EDGE,"E2");var subQ6=sQuery(id+"F0.wireOp",EDGE,"E1");var subQ7=makeQuery(id+"F1.opExtrude","CAP_FACE",FACE,{"disambiguationData":[OSD([subQ1,subQ6,subQ5,subQ4,subQ2,subQ3,subQ0])],"isStart":false});var subQ8=makeQuery(id+"F1.opExtrude","SWEPT_EDGE",EDGE,{"disambiguationData":[OSD([subQ1,subQ0])]});Q14=makeQuery(id+"F13.boolean.opBoolean","SPLIT",EDGE,{"disambiguationData":[TD([makeQuery(id+"F13.opExtrude","SWEPT_FACE",FACE,{"disambiguationData":[OSD([sQuery(id+"F12.wireOp",EDGE,"E13.left")])]})])],"derivedFrom":makeQuery(id+"F7.boolean.opBoolean","MERGE",EDGE,{"derivedFrom":[makeQuery(id+"F6.opShell","OFFSET_EDGE",EDGE,{"disambiguationData":[OSD([subQ1,subQ0])]})],"fromTools":[makeQuery(id+"F7.opExtrude","SWEPT_EDGE",EDGE,{"disambiguationData":[OSD([subQ1,subQ6,subQ5,subQ4,subQ2,subQ3,subQ0]),TDD([makeQuery(id+"F6.opShell","OFFSET_VERTEX",VERTEX,{"disambiguationData":[OSD([subQ1,subQ6,subQ5,subQ4,subQ2,subQ3,subQ0]),TDD([makeQuery(id+"F5.opFillet","BLEND_VERTEX",VERTEX,{"blendedFrom":[subQ8,makeQuery(id+"F1.opExtrude","SWEPT_FACE",FACE,{"disambiguationData":[OSD([subQ1])]}),subQ7],"blendedInto":[makeQuery(id+"F1.opExtrude","SWEPT_FACE",FACE,{"disambiguationData":[OSD([subQ1])]}),subQ7]}),makeQuery(id+"F5.opFillet","BLEND_VERTEX",VERTEX,{"blendedFrom":[subQ8,makeQuery(id+"F1.opExtrude","SWEPT_FACE",FACE,{"disambiguationData":[OSD([subQ0])]}),subQ7],"blendedInto":[makeQuery(id+"F1.opExtrude","SWEPT_FACE",FACE,{"disambiguationData":[OSD([subQ0])]}),subQ7]})])]})])]})]})});}
            var Q15;
            Q15=makeQuery(id+"F9.opExtrude","SWEPT_EDGE",EDGE,{"disambiguationData":[OSD([sQuery(id+"F0.wireOp",EDGE,"E6"),sQuery(id+"F8.wireOp",EDGE,"E9.left")])]});
            var Q16;
            Q16=makeQuery(id+"F9.opExtrude","SWEPT_EDGE",EDGE,{"disambiguationData":[OSD([sQuery(id+"F0.wireOp",EDGE,"E6"),sQuery(id+"F8.wireOp",EDGE,"E9.right")])]});
            var Q17;
            {var subQ0=sQuery(id+"F0.wireOp",EDGE,"E3");var subQ1=sQuery(id+"F0.wireOp",EDGE,"E6");var subQ2=sQuery(id+"F0.wireOp",EDGE,"E5");var subQ3=sQuery(id+"F0.wireOp",EDGE,"E4");var subQ4=sQuery(id+"F0.wireOp",EDGE,"E2");var subQ5=sQuery(id+"F0.wireOp",EDGE,"E1");var subQ6=sQuery(id+"F0.wireOp",EDGE,"E0");var subQ7=makeQuery(id+"F1.opExtrude","CAP_FACE",FACE,{"disambiguationData":[OSD([subQ6,subQ5,subQ4,subQ0,subQ3,subQ2,subQ1])],"isStart":false});var subQ8=makeQuery(id+"F1.opExtrude","SWEPT_EDGE",EDGE,{"disambiguationData":[OSD([subQ4,subQ0])]});Q17=makeQuery(id+"F13.boolean.opBoolean","SPLIT",EDGE,{"disambiguationData":[TD([makeQuery(id+"F13.opExtrude","SWEPT_FACE",FACE,{"disambiguationData":[OSD([sQuery(id+"F12.wireOp",EDGE,"E13.left")])]})])],"derivedFrom":makeQuery(id+"F7.boolean.opBoolean","MERGE",EDGE,{"derivedFrom":[makeQuery(id+"F6.opShell","OFFSET_EDGE",EDGE,{"disambiguationData":[OSD([subQ4,subQ0])]})],"fromTools":[makeQuery(id+"F7.opExtrude","SWEPT_EDGE",EDGE,{"disambiguationData":[OSD([subQ6,subQ5,subQ4,subQ0,subQ3,subQ2,subQ1]),TDD([makeQuery(id+"F6.opShell","OFFSET_VERTEX",VERTEX,{"disambiguationData":[OSD([subQ6,subQ5,subQ4,subQ0,subQ3,subQ2,subQ1]),TDD([makeQuery(id+"F5.opFillet","BLEND_VERTEX",VERTEX,{"blendedFrom":[subQ8,makeQuery(id+"F1.opExtrude","SWEPT_FACE",FACE,{"disambiguationData":[OSD([subQ0])]}),subQ7],"blendedInto":[makeQuery(id+"F1.opExtrude","SWEPT_FACE",FACE,{"disambiguationData":[OSD([subQ0])]}),subQ7]}),makeQuery(id+"F5.opFillet","BLEND_VERTEX",VERTEX,{"blendedFrom":[subQ8,subQ7,makeQuery(id+"F1.opExtrude","SWEPT_FACE",FACE,{"disambiguationData":[OSD([subQ4])]})],"blendedInto":[subQ7,makeQuery(id+"F1.opExtrude","SWEPT_FACE",FACE,{"disambiguationData":[OSD([subQ4])]})]})])]})])]})]})});}
            fillet(context, id + "F17", {"entities" : qUnion([Q0, Q1, Q2, Q3, Q4, Q5, Q6, Q7, Q8, Q9, Q10, Q11, Q12, Q13, Q14, Q15, Q16, Q17]), "radius" : 0.5 * mm, "tangentPropagation" : true, "allowEdgeOverflow" : false});
        }
        {
            var Q0;
            {var subQ0=sQuery(id+"F0.wireOp",EDGE,"E3");Q0=makeQuery(id+"F13.boolean.opBoolean","INTERSECT",EDGE,{"derivedFrom":[makeQuery(id+"F7.boolean.opBoolean","MERGE",FACE,{"derivedFrom":[makeQuery(id+"F6.opShell","OFFSET_FACE",FACE,{"disambiguationData":[OSD([subQ0])]})],"fromTools":[makeQuery(id+"F7.opExtrude","SWEPT_FACE",FACE,{"disambiguationData":[OSD([subQ0]),TDD([makeQuery(id+"F6.opShell","OFFSET_EDGE",EDGE,{"disambiguationData":[OSD([subQ0]),TDD([makeQuery(id+"F1.opExtrude","CAP_EDGE",EDGE,{"disambiguationData":[OSD([subQ0])],"isStart":false})])]})])]})]}),makeQuery(id+"F13.opExtrude","SWEPT_FACE",FACE,{"disambiguationData":[OSD([sQuery(id+"F12.wireOp",EDGE,"E13.left")])]})]});}
            var Q1;
            Q1=makeQuery(id+"F9.opExtrude","CAP_EDGE",EDGE,{"disambiguationData":[OSD([sQuery(id+"F8.wireOp",EDGE,"E9.left")]),topologyDisambiguationEdgeConnected([makeQuery(id+"F6.opShell","OFFSET_FACE",FACE,{"disambiguationData":[OSD([sQuery(id+"F3.hole-0.sketch.wireOp",EDGE,"core_line_2")])]})])],"isStart":false});
            var Q2;
            Q2=makeQuery(id+"F9.opExtrude","CAP_EDGE",EDGE,{"disambiguationData":[OSD([sQuery(id+"F8.wireOp",EDGE,"E9.right")]),topologyDisambiguationEdgeConnected([makeQuery(id+"F6.opShell","OFFSET_FACE",FACE,{"disambiguationData":[OSD([sQuery(id+"F3.hole-0.sketch.wireOp",EDGE,"core_line_2")])]})])],"isStart":false});
            var Q3;
            {var subQ0=sQuery(id+"F3.hole-0.sketch.wireOp",EDGE,"csink_start_line_1");var subQ2=sQuery(id+"F3.hole-0.sketch.wireOp",EDGE,"core_line_2");var subQ4=makeQuery(id+"F9.opExtrude","SWEPT_FACE",FACE,{"disambiguationData":[OSD([sQuery(id+"F8.wireOp",EDGE,"E9.right")])]});Q3=makeQuery(id+"F13.boolean.opBoolean","SPLIT",EDGE,{"disambiguationData":[TD([subQ4])],"derivedFrom":makeQuery(id+"F11.boolean.opBoolean","SPLIT",EDGE,{"disambiguationData":[TD([subQ4])],"derivedFrom":makeQuery(id+"F6.opShell","OFFSET_EDGE",EDGE,{"disambiguationData":[OSD([subQ0,subQ2])]})})});}
            var Q4;
            {var subQ0=sQuery(id+"F3.hole-0.sketch.wireOp",EDGE,"csink_start_line_1");var subQ3=makeQuery(id+"F9.opExtrude","SWEPT_FACE",FACE,{"disambiguationData":[OSD([sQuery(id+"F8.wireOp",EDGE,"E9.right")])]});Q4=makeQuery(id+"F13.boolean.opBoolean","SPLIT",EDGE,{"disambiguationData":[TD([subQ3])],"derivedFrom":makeQuery(id+"F11.boolean.opBoolean","SPLIT",EDGE,{"disambiguationData":[TD([subQ3])],"derivedFrom":makeQuery(id+"F6.opShell","OFFSET_EDGE",EDGE,{"disambiguationData":[OSD([subQ0,sQuery(id+"F3.hole-0.sketch.wireOp",EDGE,"csink_start_line_2")])]})})});}
            var Q5;
            {var subQ0=sQuery(id+"F3.hole-0.sketch.wireOp",EDGE,"csink_start_line_1");var subQ2=makeQuery(id+"F9.opExtrude","SWEPT_FACE",FACE,{"disambiguationData":[OSD([sQuery(id+"F8.wireOp",EDGE,"E9.left")])]});var subQ3=sQuery(id+"F3.hole-0.sketch.wireOp",EDGE,"core_line_2");Q5=makeQuery(id+"F16.boolean.opBoolean","SPLIT",EDGE,{"disambiguationData":[TD([subQ2])],"derivedFrom":makeQuery(id+"F11.boolean.opBoolean","SPLIT",EDGE,{"disambiguationData":[TD([subQ2])],"derivedFrom":makeQuery(id+"F6.opShell","OFFSET_EDGE",EDGE,{"disambiguationData":[OSD([subQ0,subQ3])]})})});}
            var Q6;
            {var subQ0=sQuery(id+"F3.hole-0.sketch.wireOp",EDGE,"csink_start_line_1");var subQ2=makeQuery(id+"F9.opExtrude","SWEPT_FACE",FACE,{"disambiguationData":[OSD([sQuery(id+"F8.wireOp",EDGE,"E9.left")])]});Q6=makeQuery(id+"F16.boolean.opBoolean","SPLIT",EDGE,{"disambiguationData":[TD([subQ2])],"derivedFrom":makeQuery(id+"F11.boolean.opBoolean","SPLIT",EDGE,{"disambiguationData":[TD([subQ2])],"derivedFrom":makeQuery(id+"F6.opShell","OFFSET_EDGE",EDGE,{"disambiguationData":[OSD([subQ0,sQuery(id+"F3.hole-0.sketch.wireOp",EDGE,"csink_start_line_2")])]})})});}
            var Q7;
            {var subQ1=sQuery(id+"F0.wireOp",EDGE,"E5");var subQ2=sQuery(id+"F0.wireOp",EDGE,"E4");Q7=makeQuery(id+"F16.boolean.opBoolean","INTERSECT",EDGE,{"derivedFrom":[makeQuery(id+"F11.boolean.opBoolean","SPLIT",FACE,{"disambiguationData":[TD([makeQuery(id+"F6.opShell","OFFSET_FACE",FACE,{"disambiguationData":[OSD([subQ1])]})])],"derivedFrom":makeQuery(id+"F7.boolean.opBoolean","MERGE",FACE,{"derivedFrom":[makeQuery(id+"F6.opShell","OFFSET_FACE",FACE,{"disambiguationData":[OSD([subQ2])]})],"fromTools":[makeQuery(id+"F7.opExtrude","SWEPT_FACE",FACE,{"disambiguationData":[OSD([subQ2]),TDD([makeQuery(id+"F6.opShell","OFFSET_EDGE",EDGE,{"disambiguationData":[OSD([subQ2]),TDD([makeQuery(id+"F1.opExtrude","CAP_EDGE",EDGE,{"disambiguationData":[OSD([subQ2])],"isStart":false})])]})])]})]})}),makeQuery(id+"F16.opExtrude","SWEPT_FACE",FACE,{"disambiguationData":[OSD([sQuery(id+"F15.wireOp",EDGE,"E14.right")])]})]});}
            var Q8;
            Q8=makeQuery(id+"F16.boolean.opBoolean","INTERSECT",EDGE,{"derivedFrom":[makeQuery(id+"F11.boolean.opBoolean","SPLIT",FACE,{"disambiguationData":[TD([makeQuery(id+"F9.opExtrude","SWEPT_FACE",FACE,{"disambiguationData":[OSD([sQuery(id+"F8.wireOp",EDGE,"E9.left")])]})])],"derivedFrom":makeQuery(id+"F6.opShell","OFFSET_FACE",FACE,{"disambiguationData":[OSD([sQuery(id+"F3.hole-0.sketch.wireOp",EDGE,"core_line_2")])]})}),makeQuery(id+"F16.opExtrude","SWEPT_FACE",FACE,{"disambiguationData":[OSD([sQuery(id+"F15.wireOp",EDGE,"E14.right")])]})]});
            var Q9;
            Q9=makeQuery(id+"F13.boolean.opBoolean","INTERSECT",EDGE,{"derivedFrom":[makeQuery(id+"F11.boolean.opBoolean","SPLIT",FACE,{"disambiguationData":[TD([makeQuery(id+"F9.opExtrude","SWEPT_FACE",FACE,{"disambiguationData":[OSD([sQuery(id+"F8.wireOp",EDGE,"E9.right")])]})])],"derivedFrom":makeQuery(id+"F6.opShell","OFFSET_FACE",FACE,{"disambiguationData":[OSD([sQuery(id+"F3.hole-0.sketch.wireOp",EDGE,"core_line_2")])]})}),makeQuery(id+"F13.opExtrude","SWEPT_FACE",FACE,{"disambiguationData":[OSD([sQuery(id+"F12.wireOp",EDGE,"E13.left")])]})]});
            var Q10;
            Q10=makeQuery(id+"F16.opExtrude","SWEPT_FACE",FACE,{"disambiguationData":[OSD([sQuery(id+"F15.wireOp",EDGE,"E14.left")])]});
            var Q11;
            Q11=makeQuery(id+"F13.boolean.opBoolean","SPLIT",FACE,{"disambiguationData":[TD([makeQuery(id+"F6.opShell","OFFSET_FACE",FACE,{"disambiguationData":[OSD([sQuery(id+"F3.hole-0.sketch.wireOp",EDGE,"csink_start_line_1")])]})])],"derivedFrom":makeQuery(id+"F13.opExtrude","SWEPT_FACE",FACE,{"disambiguationData":[OSD([sQuery(id+"F12.wireOp",EDGE,"E13.right")])]})});
            var Q12;
            Q12=makeQuery(id+"F11.opExtrude","CAP_EDGE",EDGE,{"disambiguationData":[OSD([sQuery(id+"F10.wireOp",EDGE,"E12.left")]),topologyDisambiguationEdgeConnected([makeQuery(id+"F6.opShell","OFFSET_FACE",FACE,{"disambiguationData":[OSD([sQuery(id+"F3.hole-0.sketch.wireOp",EDGE,"core_line_2")])]})])],"isStart":false});
            var Q13;
            Q13=makeQuery(id+"F11.opExtrude","CAP_EDGE",EDGE,{"disambiguationData":[OSD([sQuery(id+"F10.wireOp",EDGE,"E12.right")]),topologyDisambiguationEdgeConnected([makeQuery(id+"F6.opShell","OFFSET_FACE",FACE,{"disambiguationData":[OSD([sQuery(id+"F3.hole-0.sketch.wireOp",EDGE,"core_line_2")])]})])],"isStart":false});
            var Q14;
            {var subQ0=sQuery(id+"F3.hole-0.sketch.wireOp",EDGE,"csink_start_line_1");var subQ2=sQuery(id+"F3.hole-0.sketch.wireOp",EDGE,"core_line_2");var subQ4=makeQuery(id+"F11.opExtrude","SWEPT_FACE",FACE,{"disambiguationData":[OSD([sQuery(id+"F10.wireOp",EDGE,"E12.right")])]});Q14=makeQuery(id+"F16.boolean.opBoolean","SPLIT",EDGE,{"disambiguationData":[TD([subQ4])],"derivedFrom":makeQuery(id+"F11.boolean.opBoolean","SPLIT",EDGE,{"disambiguationData":[TD([makeQuery(id+"F9.opExtrude","SWEPT_FACE",FACE,{"disambiguationData":[OSD([sQuery(id+"F8.wireOp",EDGE,"E9.left")])]})])],"derivedFrom":makeQuery(id+"F6.opShell","OFFSET_EDGE",EDGE,{"disambiguationData":[OSD([subQ0,subQ2])]})})});}
            var Q15;
            {var subQ0=sQuery(id+"F3.hole-0.sketch.wireOp",EDGE,"csink_start_line_1");var subQ3=makeQuery(id+"F11.opExtrude","SWEPT_FACE",FACE,{"disambiguationData":[OSD([sQuery(id+"F10.wireOp",EDGE,"E12.right")])]});Q15=makeQuery(id+"F16.boolean.opBoolean","SPLIT",EDGE,{"disambiguationData":[TD([subQ3])],"derivedFrom":makeQuery(id+"F11.boolean.opBoolean","SPLIT",EDGE,{"disambiguationData":[TD([makeQuery(id+"F9.opExtrude","SWEPT_FACE",FACE,{"disambiguationData":[OSD([sQuery(id+"F8.wireOp",EDGE,"E9.left")])]})])],"derivedFrom":makeQuery(id+"F6.opShell","OFFSET_EDGE",EDGE,{"disambiguationData":[OSD([subQ0,sQuery(id+"F3.hole-0.sketch.wireOp",EDGE,"csink_start_line_2")])]})})});}
            var Q16;
            {var subQ0=sQuery(id+"F3.hole-0.sketch.wireOp",EDGE,"csink_start_line_1");var subQ3=makeQuery(id+"F11.opExtrude","SWEPT_FACE",FACE,{"disambiguationData":[OSD([sQuery(id+"F10.wireOp",EDGE,"E12.left")])]});Q16=makeQuery(id+"F13.boolean.opBoolean","SPLIT",EDGE,{"disambiguationData":[TD([subQ3])],"derivedFrom":makeQuery(id+"F11.boolean.opBoolean","SPLIT",EDGE,{"disambiguationData":[TD([makeQuery(id+"F9.opExtrude","SWEPT_FACE",FACE,{"disambiguationData":[OSD([sQuery(id+"F8.wireOp",EDGE,"E9.right")])]})])],"derivedFrom":makeQuery(id+"F6.opShell","OFFSET_EDGE",EDGE,{"disambiguationData":[OSD([subQ0,sQuery(id+"F3.hole-0.sketch.wireOp",EDGE,"csink_start_line_2")])]})})});}
            var Q17;
            {var subQ0=sQuery(id+"F3.hole-0.sketch.wireOp",EDGE,"csink_start_line_1");var subQ2=sQuery(id+"F3.hole-0.sketch.wireOp",EDGE,"core_line_2");var subQ4=makeQuery(id+"F11.opExtrude","SWEPT_FACE",FACE,{"disambiguationData":[OSD([sQuery(id+"F10.wireOp",EDGE,"E12.left")])]});Q17=makeQuery(id+"F13.boolean.opBoolean","SPLIT",EDGE,{"disambiguationData":[TD([subQ4])],"derivedFrom":makeQuery(id+"F11.boolean.opBoolean","SPLIT",EDGE,{"disambiguationData":[TD([makeQuery(id+"F9.opExtrude","SWEPT_FACE",FACE,{"disambiguationData":[OSD([sQuery(id+"F8.wireOp",EDGE,"E9.right")])]})])],"derivedFrom":makeQuery(id+"F6.opShell","OFFSET_EDGE",EDGE,{"disambiguationData":[OSD([subQ0,subQ2])]})})});}
            fillet(context, id + "F18", {"entities" : qUnion([Q0, Q1, Q2, Q3, Q4, Q5, Q6, Q7, Q8, Q9, Q10, Q11, Q12, Q13, Q14, Q15, Q16, Q17]), "radius" : 1 * mm, "tangentPropagation" : true, "allowEdgeOverflow" : false});
        }
        {
            var Q0;
            {var subQ0=sQuery(id+"F0.wireOp",EDGE,"E6");var subQ1=sQuery(id+"F0.wireOp",EDGE,"E0");Q0=makeQuery(id+"F5.opFillet","BLEND_EDGE",EDGE,{"blendedFrom":[makeQuery(id+"F1.opExtrude","SWEPT_EDGE",EDGE,{"disambiguationData":[OSD([subQ1,subQ0])]}),makeQuery(id+"F1.opExtrude","CAP_FACE",FACE,{"disambiguationData":[OSD([subQ1,sQuery(id+"F0.wireOp",EDGE,"E1"),sQuery(id+"F0.wireOp",EDGE,"E2"),sQuery(id+"F0.wireOp",EDGE,"E3"),sQuery(id+"F0.wireOp",EDGE,"E4"),sQuery(id+"F0.wireOp",EDGE,"E5"),subQ0])],"isStart":true})],"blendedInto":[makeQuery(id+"F1.opExtrude","CAP_FACE",FACE,{"disambiguationData":[OSD([subQ1,sQuery(id+"F0.wireOp",EDGE,"E1"),sQuery(id+"F0.wireOp",EDGE,"E2"),sQuery(id+"F0.wireOp",EDGE,"E3"),sQuery(id+"F0.wireOp",EDGE,"E4"),sQuery(id+"F0.wireOp",EDGE,"E5"),subQ0])],"isStart":true})]});}
            var Q1;
            {var subQ0=sQuery(id+"F0.wireOp",EDGE,"E6");var subQ1=sQuery(id+"F0.wireOp",EDGE,"E0");Q1=makeQuery(id+"F5.opFillet","BLEND_EDGE",EDGE,{"blendedFrom":[makeQuery(id+"F1.opExtrude","SWEPT_EDGE",EDGE,{"disambiguationData":[OSD([subQ1,subQ0])]}),makeQuery(id+"F1.opExtrude","CAP_FACE",FACE,{"disambiguationData":[OSD([subQ1,sQuery(id+"F0.wireOp",EDGE,"E1"),sQuery(id+"F0.wireOp",EDGE,"E2"),sQuery(id+"F0.wireOp",EDGE,"E3"),sQuery(id+"F0.wireOp",EDGE,"E4"),sQuery(id+"F0.wireOp",EDGE,"E5"),subQ0])],"isStart":false})],"blendedInto":[makeQuery(id+"F1.opExtrude","CAP_FACE",FACE,{"disambiguationData":[OSD([subQ1,sQuery(id+"F0.wireOp",EDGE,"E1"),sQuery(id+"F0.wireOp",EDGE,"E2"),sQuery(id+"F0.wireOp",EDGE,"E3"),sQuery(id+"F0.wireOp",EDGE,"E4"),sQuery(id+"F0.wireOp",EDGE,"E5"),subQ0])],"isStart":false})]});}
            var Q2;
            {var subQ0=sQuery(id+"F0.wireOp",EDGE,"E4");var subQ1=sQuery(id+"F0.wireOp",EDGE,"E3");Q2=makeQuery(id+"F9.boolean.opBoolean","SPLIT",EDGE,{"disambiguationData":[TD([makeQuery(id+"F6.opShell","OFFSET_FACE",FACE,{"disambiguationData":[OSD([subQ1])]})])],"derivedFrom":makeQuery(id+"F6.opShell","OFFSET_EDGE",EDGE,{"disambiguationData":[OSD([subQ0]),TDD([makeQuery(id+"F1.opExtrude","CAP_EDGE",EDGE,{"disambiguationData":[OSD([subQ0])],"isStart":true})])]})});}
            var Q3;
            {var subQ0=sQuery(id+"F8.wireOp",EDGE,"E9.left");var subQ1=sQuery(id+"F0.wireOp",EDGE,"E6");var subQ2=sQuery(id+"F0.wireOp",EDGE,"E4");Q3=makeQuery(id+"F17.opFillet","BLEND_EDGE",EDGE,{"blendedFrom":[makeQuery(id+"F9.opExtrude","SWEPT_EDGE",EDGE,{"disambiguationData":[OSD([subQ1,subQ0])]}),makeQuery(id+"F9.boolean.opBoolean","MERGE",FACE,{"derivedFrom":[makeQuery(id+"F1.opExtrude","CAP_FACE",FACE,{"disambiguationData":[OSD([sQuery(id+"F0.wireOp",EDGE,"E0"),sQuery(id+"F0.wireOp",EDGE,"E1"),sQuery(id+"F0.wireOp",EDGE,"E2"),sQuery(id+"F0.wireOp",EDGE,"E3"),subQ2,sQuery(id+"F0.wireOp",EDGE,"E5"),subQ1])],"isStart":true}),makeQuery(id+"F9.opExtrude","CAP_FACE",FACE,{"disambiguationData":[OSD([subQ2,subQ1,subQ0,sQuery(id+"F8.wireOp",EDGE,"E9.right")])],"isStart":true})]})],"blendedInto":[makeQuery(id+"F9.boolean.opBoolean","MERGE",FACE,{"derivedFrom":[makeQuery(id+"F1.opExtrude","CAP_FACE",FACE,{"disambiguationData":[OSD([sQuery(id+"F0.wireOp",EDGE,"E0"),sQuery(id+"F0.wireOp",EDGE,"E1"),sQuery(id+"F0.wireOp",EDGE,"E2"),sQuery(id+"F0.wireOp",EDGE,"E3"),subQ2,sQuery(id+"F0.wireOp",EDGE,"E5"),subQ1])],"isStart":true}),makeQuery(id+"F9.opExtrude","CAP_FACE",FACE,{"disambiguationData":[OSD([subQ2,subQ1,subQ0,sQuery(id+"F8.wireOp",EDGE,"E9.right")])],"isStart":true})]})]});}
            var Q4;
            {var subQ0=sQuery(id+"F0.wireOp",EDGE,"E6");var subQ1=sQuery(id+"F0.wireOp",EDGE,"E5");var subQ2=sQuery(id+"F0.wireOp",EDGE,"E4");var subQ3=sQuery(id+"F0.wireOp",EDGE,"E3");var subQ4=sQuery(id+"F0.wireOp",EDGE,"E2");var subQ5=sQuery(id+"F0.wireOp",EDGE,"E1");var subQ6=sQuery(id+"F0.wireOp",EDGE,"E0");var subQ7=makeQuery(id+"F11.opExtrude","CAP_FACE",FACE,{"disambiguationData":[OSD([subQ6,subQ5,subQ4,subQ3,subQ2,subQ1,subQ0,sQuery(id+"F10.wireOp",EDGE,"E12.left"),sQuery(id+"F10.wireOp",EDGE,"E12.right")])],"isStart":true});var subQ8=makeQuery(id+"F1.opExtrude","CAP_FACE",FACE,{"disambiguationData":[OSD([subQ6,subQ5,subQ4,subQ3,subQ2,subQ1,subQ0])],"isStart":false});var subQ9=subQ8;var subQ10=makeQuery(id+"F1.opExtrude","SWEPT_EDGE",EDGE,{"disambiguationData":[OSD([subQ1,subQ0])]});Q4=makeQuery(id+"F17.opFillet","BLEND_EDGE",EDGE,{"blendedFrom":[makeQuery(id+"F16.boolean.opBoolean","SPLIT",EDGE,{"disambiguationData":[TD([makeQuery(id+"F16.opExtrude","SWEPT_FACE",FACE,{"disambiguationData":[OSD([sQuery(id+"F15.wireOp",EDGE,"E14.left")])]})])],"derivedFrom":makeQuery(id+"F7.boolean.opBoolean","MERGE",EDGE,{"derivedFrom":[makeQuery(id+"F6.opShell","OFFSET_EDGE",EDGE,{"disambiguationData":[OSD([subQ1,subQ0])]})],"fromTools":[makeQuery(id+"F7.opExtrude","SWEPT_EDGE",EDGE,{"disambiguationData":[OSD([subQ6,subQ5,subQ4,subQ3,subQ2,subQ1,subQ0]),TDD([makeQuery(id+"F6.opShell","OFFSET_VERTEX",VERTEX,{"disambiguationData":[OSD([subQ6,subQ5,subQ4,subQ3,subQ2,subQ1,subQ0]),TDD([makeQuery(id+"F5.opFillet","BLEND_VERTEX",VERTEX,{"blendedFrom":[subQ10,makeQuery(id+"F1.opExtrude","SWEPT_FACE",FACE,{"disambiguationData":[OSD([subQ1])]}),subQ9],"blendedInto":[makeQuery(id+"F1.opExtrude","SWEPT_FACE",FACE,{"disambiguationData":[OSD([subQ1])]}),subQ9]}),makeQuery(id+"F5.opFillet","BLEND_VERTEX",VERTEX,{"blendedFrom":[subQ10,makeQuery(id+"F1.opExtrude","SWEPT_FACE",FACE,{"disambiguationData":[OSD([subQ0])]}),subQ9],"blendedInto":[makeQuery(id+"F1.opExtrude","SWEPT_FACE",FACE,{"disambiguationData":[OSD([subQ0])]}),subQ9]})])]})])]})]})}),makeQuery(id+"F11.boolean.opBoolean","MERGE",FACE,{"derivedFrom":[subQ9,subQ7]})],"blendedInto":[makeQuery(id+"F11.boolean.opBoolean","MERGE",FACE,{"derivedFrom":[subQ9,subQ7]})]});}
            var Q5;
            {var subQ0=sQuery(id+"F10.wireOp",EDGE,"E12.left");var subQ1=sQuery(id+"F0.wireOp",EDGE,"E6");var subQ2=sQuery(id+"F0.wireOp",EDGE,"E5");var subQ3=sQuery(id+"F0.wireOp",EDGE,"E4");var subQ4=sQuery(id+"F0.wireOp",EDGE,"E3");var subQ5=sQuery(id+"F0.wireOp",EDGE,"E2");var subQ6=sQuery(id+"F0.wireOp",EDGE,"E1");var subQ7=sQuery(id+"F0.wireOp",EDGE,"E0");var subQ8=makeQuery(id+"F1.opExtrude","CAP_FACE",FACE,{"disambiguationData":[OSD([subQ7,subQ6,subQ5,subQ4,subQ3,subQ2,subQ1])],"isStart":false});Q5=makeQuery(id+"F17.opFillet","BLEND_EDGE",EDGE,{"blendedFrom":[makeQuery(id+"F11.opExtrude","SWEPT_EDGE",EDGE,{"disambiguationData":[OSD([subQ7,subQ6,subQ5,subQ4,subQ3,subQ2,subQ1,subQ0]),TDD([makeQuery(id+"F10.imprint","INTERSECT",VERTEX,{"derivedFrom":[makeQuery(id+"F7.boolean.opBoolean","INTERSECT",EDGE,{"derivedFrom":[subQ8,makeQuery(id+"F7.opExtrude","CAP_FACE",FACE,{"disambiguationData":[OSD([subQ7,subQ6,subQ5,subQ4,subQ3,subQ2,subQ1]),TDD([subQ8])],"isStart":true}),makeQuery(id+"F7.opExtrude","SWEPT_FACE",FACE,{"disambiguationData":[OSD([subQ1]),TDD([makeQuery(id+"F6.opShell","OFFSET_EDGE",EDGE,{"disambiguationData":[OSD([subQ1]),TDD([makeQuery(id+"F1.opExtrude","CAP_EDGE",EDGE,{"disambiguationData":[OSD([subQ1])],"isStart":false})])]})])]})]}),subQ0]})])]}),makeQuery(id+"F11.boolean.opBoolean","MERGE",FACE,{"derivedFrom":[subQ8,makeQuery(id+"F11.opExtrude","CAP_FACE",FACE,{"disambiguationData":[OSD([subQ7,subQ6,subQ5,subQ4,subQ3,subQ2,subQ1,subQ0,sQuery(id+"F10.wireOp",EDGE,"E12.right")])],"isStart":true})]})],"blendedInto":[makeQuery(id+"F11.boolean.opBoolean","MERGE",FACE,{"derivedFrom":[subQ8,makeQuery(id+"F11.opExtrude","CAP_FACE",FACE,{"disambiguationData":[OSD([subQ7,subQ6,subQ5,subQ4,subQ3,subQ2,subQ1,subQ0,sQuery(id+"F10.wireOp",EDGE,"E12.right")])],"isStart":true})]})]});}
            var Q6;
            Q6=makeQuery(id+"F3.hole-0.boolean.opBoolean","INTERSECT",EDGE,{"derivedFrom":[makeQuery(id+"F1.opExtrude","SWEPT_FACE",FACE,{"disambiguationData":[OSD([sQuery(id+"F0.wireOp",EDGE,"E6")])]}),makeQuery(id+"F3.hole-0.opRevolve","SWEPT_FACE",FACE,{"disambiguationData":[OSD([sQuery(id+"F3.hole-0.sketch.wireOp",EDGE,"core_line_2")])]})]});
            chamfer(context, id + "F19", {"entities" : qUnion([Q0, Q1, Q2, Q3, Q4, Q5, Q6]), "width" : 0.3 * mm, "tangentPropagation" : true});
        }
    });
